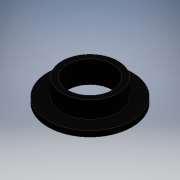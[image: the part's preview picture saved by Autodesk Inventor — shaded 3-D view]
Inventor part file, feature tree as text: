
AUTODESK INVENTOR PART (.ipt)
format: ipt  version: 2020.2 (Build 242310000, 310)  size: 104,960 bytes
history: native  units: mm
features: extrude x2, other x1, sketch x1
ambient origin geometry x8: Origin, YZ Plane, XZ Plane, XY Plane, X Axis, Y Axis, Z Axis, Center Point
bodies: Body1 (feature_tree)
feature tree (4):
  other  "ソリッド1"
  sketch  "スケッチ1"
  extrude  "押し出し1"  Depth=15.0mm
  extrude  "押し出し2"  Depth=10.0mm
